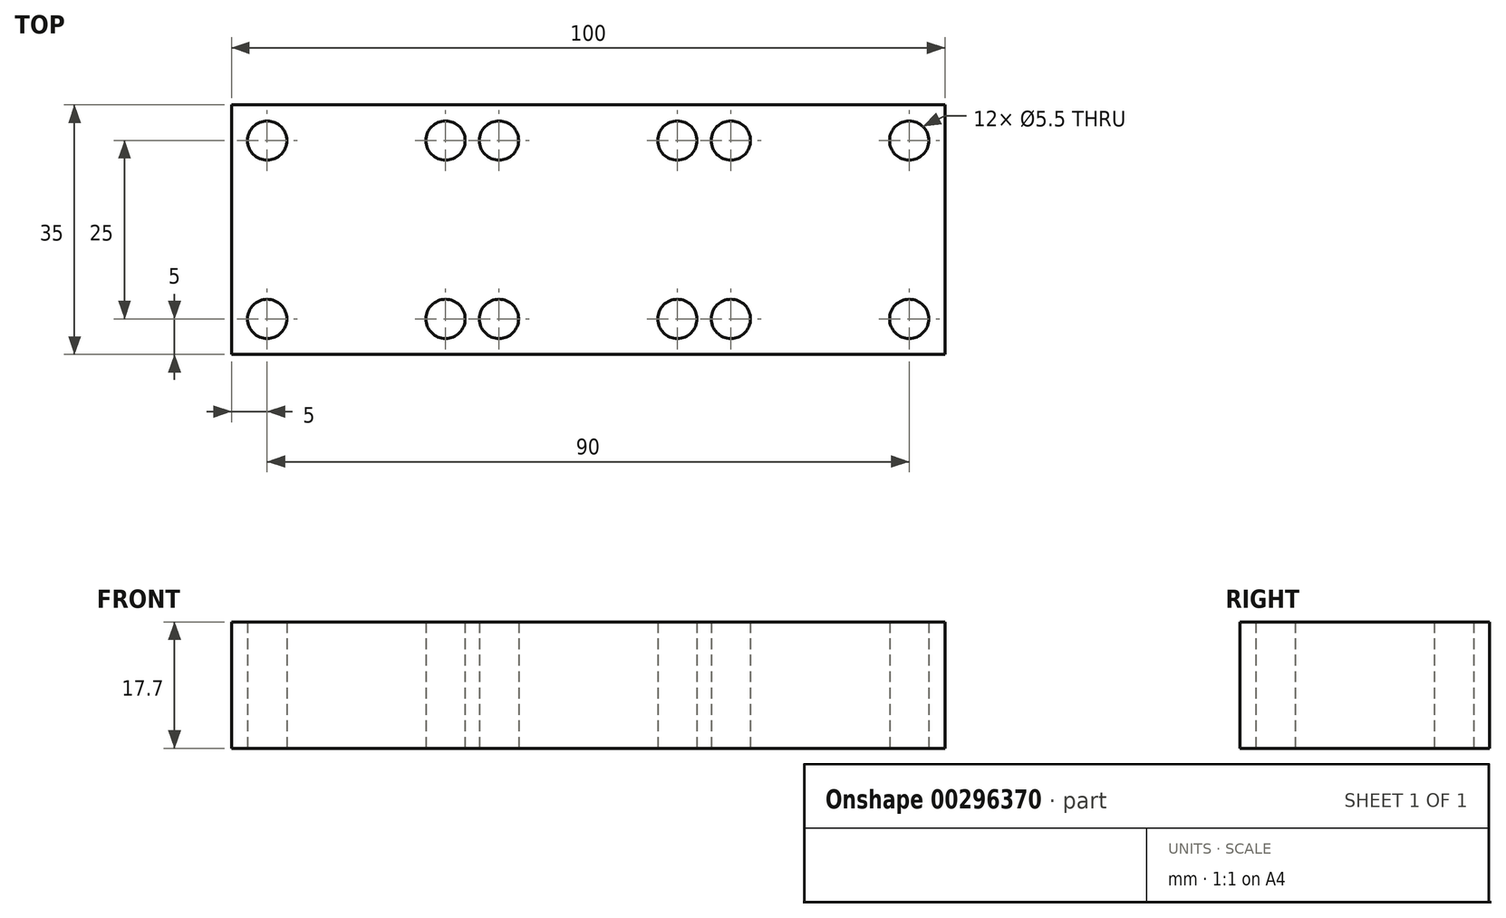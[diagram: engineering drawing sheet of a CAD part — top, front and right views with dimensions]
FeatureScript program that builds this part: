
annotation { "Feature Type Name" : "Feature", "Feature Type Description" : "" }
export const myFeature = defineFeature(function(context is Context, id is Id, definition is map)
    precondition{}
    {
        {
            var Q0;
            Q0=qCreatedBy(makeId("Top.planeOp"),FACE);
            var sketch = newSketch(context, id + "F0", { "sketchPlane" : qUnion([Q0])});
            skLineSegment(sketch, "E0.bottom", {"start": v(0, 0) * mm, "end": v(100, 0) * mm});
            skLineSegment(sketch, "E0.top", {"start": v(0, 35) * mm, "end": v(100, 35) * mm});
            skLineSegment(sketch, "E0.left", {"start": v(0, 0) * mm, "end": v(0, 35) * mm});
            skLineSegment(sketch, "E0.right", {"start": v(100, 0) * mm, "end": v(100, 35) * mm});
            skLineSegment(sketch, "E1", {"start": v(0, 17.5) * mm, "end": v(100, 17.5) * mm, "construction": true});
            skLineSegment(sketch, "E2", {"start": v(50, 35) * mm, "end": v(50, 0) * mm, "construction": true});
            skLineSegment(sketch, "E3.0", {"start": v(30, 50) * mm, "end": v(30, 0) * mm, "construction": true});
            skLineSegment(sketch, "E4.0", {"start": v(70, 50) * mm, "end": v(70, 0) * mm, "construction": true});
            skLineSegment(sketch, "E5.0", {"start": v(0, 5) * mm, "end": v(100, 5) * mm, "construction": true});
            skLineSegment(sketch, "E6.0", {"start": v(0, 30) * mm, "end": v(100, 30) * mm, "construction": true});
            skLineSegment(sketch, "E7.0", {"start": v(5, 50) * mm, "end": v(5, 0) * mm, "construction": true});
            skLineSegment(sketch, "E8.0", {"start": v(95, 50) * mm, "end": v(95, 0) * mm, "construction": true});
            skPoint(sketch, "E9", {"position": v(5, 30) * mm});
            skPoint(sketch, "E10", {"position": v(30, 30) * mm});
            skPoint(sketch, "E11", {"position": v(30, 5) * mm});
            skPoint(sketch, "E12", {"position": v(5, 5) * mm});
            skPoint(sketch, "E13", {"position": v(70, 5) * mm});
            skPoint(sketch, "E14", {"position": v(95, 5) * mm});
            skPoint(sketch, "E15", {"position": v(95, 30) * mm});
            skPoint(sketch, "E16", {"position": v(70, 30) * mm});
            skLineSegment(sketch, "E17.0", {"start": v(62.5, 50) * mm, "end": v(62.5, 0) * mm, "construction": true});
            skLineSegment(sketch, "E18.0", {"start": v(37.5, 50) * mm, "end": v(37.5, 0) * mm, "construction": true});
            skPoint(sketch, "E19", {"position": v(37.5, 30) * mm});
            skPoint(sketch, "E20", {"position": v(37.5, 5) * mm});
            skPoint(sketch, "E21", {"position": v(62.5, 5) * mm});
            skPoint(sketch, "E22", {"position": v(62.5, 30) * mm});
            skSolve(sketch);
        }
        {
            var Q0;
            Q0 = qSketchRegion(id + "F0", true);
            extrude(context, id + "F1", {"entities" : qUnion([Q0]), "depth" : (25 - 12 + 4.7) * mm});
        }
        {
            var Q0;
            Q0=sQuery(id+"F0.wireOp",VERTEX,"E9");
            var Q1;
            Q1=sQuery(id+"F0.wireOp",VERTEX,"E12");
            var Q2;
            Q2=sQuery(id+"F0.wireOp",VERTEX,"E11");
            var Q3;
            Q3=sQuery(id+"F0.wireOp",VERTEX,"E20");
            var Q4;
            Q4=sQuery(id+"F0.wireOp",VERTEX,"E19");
            var Q5;
            Q5=sQuery(id+"F0.wireOp",VERTEX,"E10");
            var Q6;
            Q6=sQuery(id+"F0.wireOp",VERTEX,"E22");
            var Q7;
            Q7=sQuery(id+"F0.wireOp",VERTEX,"E21");
            var Q8;
            Q8=sQuery(id+"F0.wireOp",VERTEX,"E13");
            var Q9;
            Q9=sQuery(id+"F0.wireOp",VERTEX,"E16");
            var Q10;
            Q10=sQuery(id+"F0.wireOp",VERTEX,"E15");
            var Q11;
            Q11=sQuery(id+"F0.wireOp",VERTEX,"E14");
            var Q12;
            Q12=makeQuery(id+"F1.opExtrude","SWEPT_BODY",BODY,{"disambiguationData":[OSD([sQuery(id+"F0.wireOp",EDGE,"E0.bottom"),sQuery(id+"F0.wireOp",EDGE,"E0.top"),sQuery(id+"F0.wireOp",EDGE,"E0.left"),sQuery(id+"F0.wireOp",EDGE,"E0.right")])]});
            hole(context, id + "F2", {"style" : HoleStyle.SIMPLE, "endStyle" : HoleEndStyle.THROUGH, "oppositeDirection" : true, "standardTappedOrClearance" : lookupTablePath({ "standard" : "ISO", "fit" : "Normal", "size" : "M5", "type" : "Clearance" }), "standardBlindInLast" : lookupTablePath({ "fit" : "Standard", "standard" : "ISO", "size" : "M5", "type" : "Clearance" }), "holeDiameter" : 5.5 * mm, "tappedDepth" : 9.6 * mm, "tapClearance" : 3, "locations" : qUnion([Q0, Q1, Q2, Q3, Q4, Q5, Q6, Q7, Q8, Q9, Q10, Q11]), "scope" : qUnion([Q12])});
        }
    });
